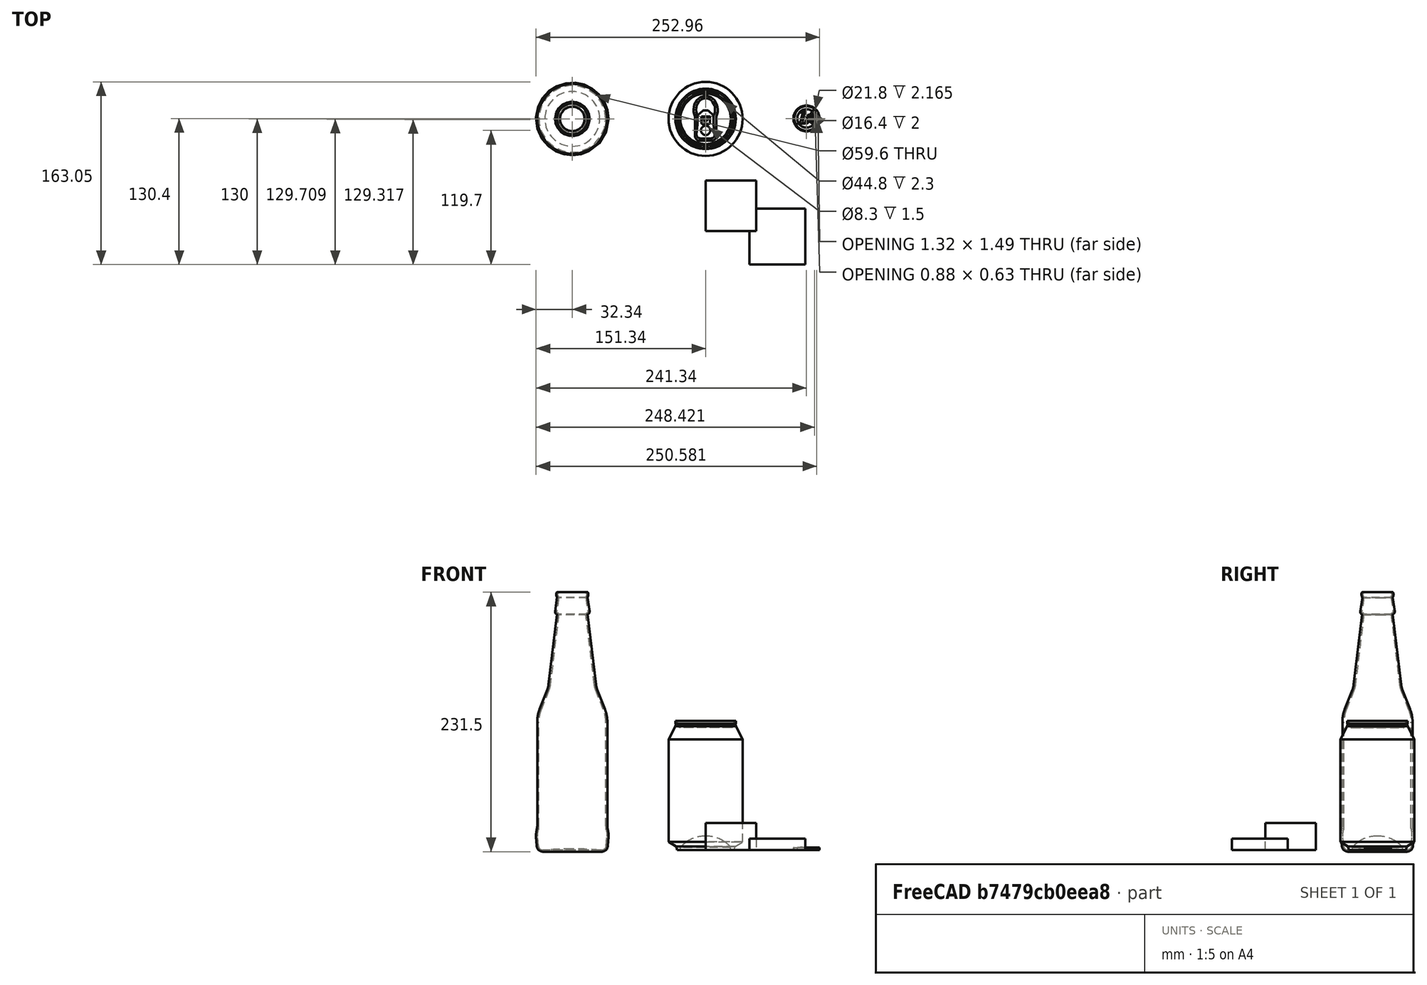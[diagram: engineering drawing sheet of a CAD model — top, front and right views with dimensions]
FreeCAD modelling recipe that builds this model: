
FCSTD DOCUMENT  (FreeCAD 1.0R38806 (Git))
Label: 03-bottle-can-euro_CON_UNION_EJEMPLO.fcstd
License: All rights reserved
LicenseURL: http://en.wikipedia.org/wiki/All_rights_reserved
objects: Part::Feature×3, Part::Box×2, Part::Fuse×1
note: 6 computed .brp shape members not serialized (recipe doc carries the construction recipe); baked Part::Feature solids carry a one-line shape summary decoded from their .brp

FEATURE [Part::Feature] Compound001  label="Euro-coin"
  Placement = pos=(90,100,0) rot=(0,0,1;0rad)
  shape: bbox 23.25 x 23.25 x 2.414 mm, 903 faces, 22 solids (baked)
FEATURE [Part::Feature] Thickness001  label="Bottle"
  Placement = pos=(-119,100,0) rot=(0,0,1;0rad)
  shape: bbox 71.75 x 74.3 x 235 mm, 40 faces (baked)
FEATURE [Part::Feature] Fusion001  label="Can"
  Placement = pos=(0,100,0) rot=(0,0,1;0rad)
  shape: bbox 66.1 x 66.1 x 115.2 mm, 53 faces (baked)
FEATURE [Part::Box] Box  label="Cube"
  AttacherType = Attacher::AttachEngine3D
  Height = 10
  Length = 50
  Placement = pos=(39,-30,0) rot=(0,0,1;0rad)
  Width = 50
FEATURE [Part::Box] Box001  label="Cube001"
  AttacherType = Attacher::AttachEngine3D
  Height = 24
  Length = 45
  Width = 45
FEATURE [Part::Fuse] Fusion
  Base = -> Box
  Refine = true
  Tool = -> Box001
